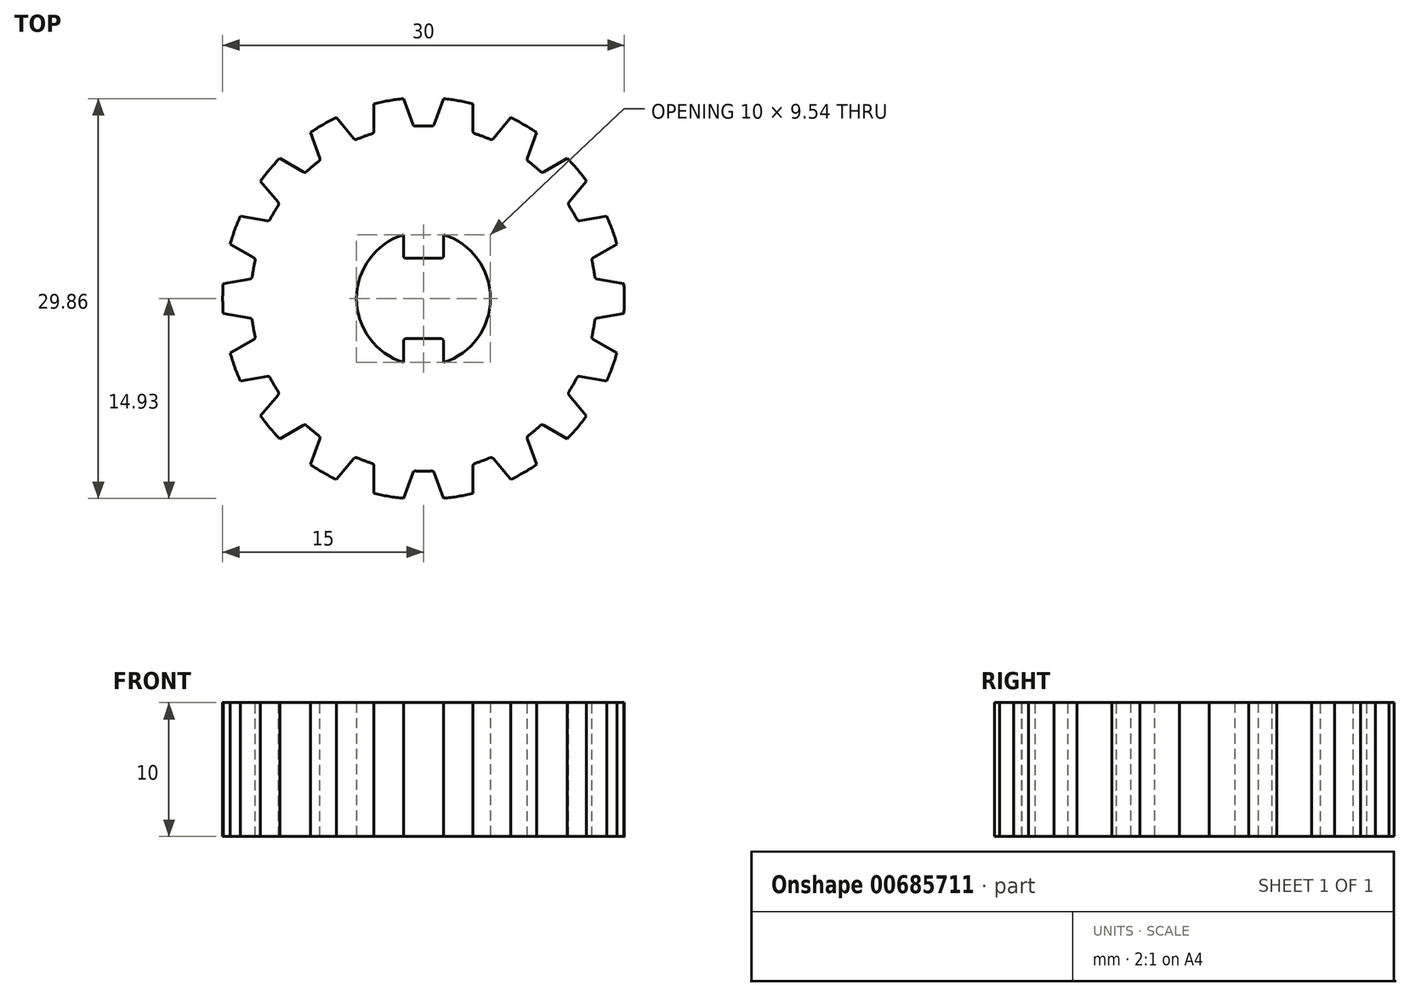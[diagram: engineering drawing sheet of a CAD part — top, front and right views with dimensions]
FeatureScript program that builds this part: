
annotation { "Feature Type Name" : "Feature", "Feature Type Description" : "" }
export const myFeature = defineFeature(function(context is Context, id is Id, definition is map)
    precondition{}
    {
        {
            var Q0;
            Q0=qCreatedBy(makeId("Top.planeOp"),FACE);
            var sketch = newSketch(context, id + "F0", { "sketchPlane" : qUnion([Q0])});
            skArc(sketch, "E0", {"start": v(1.5, -4.77) * mm, "mid": v(5, 0) * mm, "end": v(1.5, 4.77) * mm});
            skCircle(sketch, "E1", {"center": v(0, 0) * mm, "radius": 15 * mm});
            skLineSegment(sketch, "E2", {"start": v(0, -15) * mm, "end": v(0, 15) * mm, "construction": true});
            skLineSegment(sketch, "E3", {"start": v(-15, 0) * mm, "end": v(15, 0) * mm, "construction": true});
            skLineSegment(sketch, "E4", {"start": v(-1.3, -3) * mm, "end": v(1.3, -3) * mm});
            skLineSegment(sketch, "E5", {"start": v(1.5, -3.2) * mm, "end": v(1.5, -4.77) * mm});
            skLineSegment(sketch, "E6", {"start": v(-1.5, -3.2) * mm, "end": v(-1.5, -4.77) * mm});
            skPoint(sketch, "E7", {"position": v(0, -3) * mm});
            skLineSegment(sketch, "E8.MirrorCS", {"start": v(-1.3, 3) * mm, "end": v(1.3, 3) * mm});
            skLineSegment(sketch, "E9.MirrorCS", {"start": v(1.5, 3.2) * mm, "end": v(1.5, 4.77) * mm});
            skLineSegment(sketch, "E10.MirrorCS", {"start": v(-1.5, 3.2) * mm, "end": v(-1.5, 4.77) * mm});
            skArc(sketch, "E11.trimOffspring", {"start": v(-1.5, 4.77) * mm, "mid": v(-5, 0) * mm, "end": v(-1.5, -4.77) * mm});
            skPoint(sketch, "E12.visualSharp", {"position": v(-1.5, 3) * mm});
            skArc(sketch, "E12.filletArc", {"start": v(-1.5, 3.2) * mm, "mid": v(-1.44, 3.06) * mm, "end": v(-1.3, 3) * mm});
            skPoint(sketch, "E13.visualSharp", {"position": v(1.5, 3) * mm});
            skArc(sketch, "E13.filletArc", {"start": v(1.3, 3) * mm, "mid": v(1.44, 3.06) * mm, "end": v(1.5, 3.2) * mm});
            skPoint(sketch, "E14.visualSharp", {"position": v(1.5, -3) * mm});
            skArc(sketch, "E14.filletArc", {"start": v(1.5, -3.2) * mm, "mid": v(1.44, -3.06) * mm, "end": v(1.3, -3) * mm});
            skPoint(sketch, "E15.visualSharp", {"position": v(-1.5, -3) * mm});
            skArc(sketch, "E15.filletArc", {"start": v(-1.3, -3) * mm, "mid": v(-1.44, -3.06) * mm, "end": v(-1.5, -3.2) * mm});
            skSolve(sketch);
        }
        {
            var Q0;
            Q0=makeQuery(id+"F0.imprint","IMPRINT",FACE,{"disambiguationData":[TD([[makeQuery(id+"F0.imprint","IMPRINT",EDGE,{"derivedFrom":sQuery(id+"F0.wireOp",EDGE,"E0")}),-1.0]])]});
            extrude(context, id + "F1", {"entities" : qUnion([Q0]), "depth" : 10 * mm, "offsetDistance" : 25 * mm});
        }
        {
            var Q0;
            Q0=makeQuery(id+"F1.opExtrude","CAP_FACE",FACE,{"disambiguationData":[OSD([sQuery(id+"F0.wireOp",EDGE,"E0"),sQuery(id+"F0.wireOp",EDGE,"E1"),sQuery(id+"F0.wireOp",EDGE,"E4"),sQuery(id+"F0.wireOp",EDGE,"E5"),sQuery(id+"F0.wireOp",EDGE,"E6"),sQuery(id+"F0.wireOp",EDGE,"E8.MirrorCS"),sQuery(id+"F0.wireOp",EDGE,"E9.MirrorCS"),sQuery(id+"F0.wireOp",EDGE,"E10.MirrorCS"),sQuery(id+"F0.wireOp",EDGE,"E11.trimOffspring"),sQuery(id+"F0.wireOp",EDGE,"E12.filletArc"),sQuery(id+"F0.wireOp",EDGE,"E13.filletArc"),sQuery(id+"F0.wireOp",EDGE,"E14.filletArc"),sQuery(id+"F0.wireOp",EDGE,"E15.filletArc")])],"isStart":false});
            var sketch = newSketch(context, id + "F2", { "sketchPlane" : qUnion([Q0])});
            skLineSegment(sketch, "E16", {"start": v(0, 15) * mm, "end": v(0, -15) * mm, "construction": true});
            skLineSegment(sketch, "E17", {"start": v(-15, 0) * mm, "end": v(15, 0) * mm, "construction": true});
            skLineSegment(sketch, "E18", {"start": v(0.8, 13) * mm, "end": v(1.5, 14.92) * mm});
            skLineSegment(sketch, "E19.MirrorCS", {"start": v(-0.8, 13) * mm, "end": v(-1.5, 14.92) * mm});
            skArc(sketch, "E20.trimOffspring", {"start": v(0.6, 12.88) * mm, "mid": v(0, 12.9) * mm, "end": v(-0.6, 12.88) * mm});
            skPoint(sketch, "E21.visualSharp", {"position": v(-0.75, 12.87) * mm});
            skArc(sketch, "E21.filletArc", {"start": v(-0.8, 13) * mm, "mid": v(-0.72, 12.91) * mm, "end": v(-0.6, 12.88) * mm});
            skPoint(sketch, "E22.visualSharp", {"position": v(0.75, 12.87) * mm});
            skArc(sketch, "E22.filletArc", {"start": v(0.6, 12.88) * mm, "mid": v(0.72, 12.91) * mm, "end": v(0.8, 13) * mm});
            skPoint(sketch, "E23.center.orphan", {"position": v(0, 0) * mm});
            skArc(sketch, "E24.trimOffspring", {"start": v(1.5, 14.92) * mm, "mid": v(0, 15) * mm, "end": v(-1.5, 14.92) * mm});
            skSolve(sketch);
        }
        {
            var Q0;
            Q0=makeQuery(id+"F2.imprint","IMPRINT",FACE,{"disambiguationData":[TD([[makeQuery(id+"F2.imprint","IMPRINT",EDGE,{"derivedFrom":sQuery(id+"F2.wireOp",EDGE,"E18")}),1.0]])]});
            extrude(context, id + "F3", {"entities" : qUnion([Q0]), "operationType" : NewBodyOperationType.REMOVE, "endBound" : BoundingType.THROUGH_ALL, "oppositeDirection" : true, "depth" : 25 * mm, "offsetDistance" : 25 * mm});
        }
        {
            var Q0;
            Q0=makeQuery(id+"F3.boolean.opBoolean","COPY",FACE,{"derivedFrom":makeQuery(id+"F3.opExtrude","SWEPT_FACE",FACE,{"disambiguationData":[OSD([sQuery(id+"F2.wireOp",EDGE,"E19.MirrorCS")])]})});
            var Q1;
            Q1=makeQuery(id+"F3.boolean.opBoolean","COPY",FACE,{"derivedFrom":makeQuery(id+"F3.opExtrude","SWEPT_FACE",FACE,{"disambiguationData":[OSD([sQuery(id+"F2.wireOp",EDGE,"E21.filletArc")])]})});
            var Q2;
            Q2=makeQuery(id+"F3.boolean.opBoolean","COPY",FACE,{"derivedFrom":makeQuery(id+"F3.opExtrude","SWEPT_FACE",FACE,{"disambiguationData":[OSD([sQuery(id+"F2.wireOp",EDGE,"E20.trimOffspring")])]})});
            var Q3;
            Q3=makeQuery(id+"F3.boolean.opBoolean","COPY",FACE,{"derivedFrom":makeQuery(id+"F3.opExtrude","SWEPT_FACE",FACE,{"disambiguationData":[OSD([sQuery(id+"F2.wireOp",EDGE,"E22.filletArc")])]})});
            var Q4;
            Q4=makeQuery(id+"F3.boolean.opBoolean","COPY",FACE,{"derivedFrom":makeQuery(id+"F3.opExtrude","SWEPT_FACE",FACE,{"disambiguationData":[OSD([sQuery(id+"F2.wireOp",EDGE,"E18")])]})});
            var Q5;
            Q5=makeQuery(id+"F1.opExtrude","SWEPT_FACE",FACE,{"disambiguationData":[OSD([sQuery(id+"F0.wireOp",EDGE,"E1")])]});
            circularPattern(context, id + "F4", {"patternType" : PatternType.FACE, "faces" : qUnion([Q0, Q1, Q2, Q3, Q4]), "axis" : qUnion([Q5]), "angle" : 360 * degree, "instanceCount" : 18, "equalSpace" : true});
        }
    });
